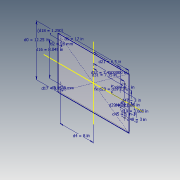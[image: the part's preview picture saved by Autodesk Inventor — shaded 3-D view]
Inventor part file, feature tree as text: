
AUTODESK INVENTOR PART (.ipt)
format: ipt  version: 2020.3 (Build 243373000, 373)  size: 146,944 bytes
history: native  units: in
note: dims shown in document units (in); Inventor stores cm internally (conversion verified against a paired STEP export)
features: hole x4, sketch x1, extrude x1, fillet x1
ambient origin geometry x8: Origin, YZ Plane, XZ Plane, XY Plane, X Axis, Y Axis, Z Axis, Center Point
bodies: Solid1 (feature_tree)
feature tree (7):
  sketch  "Sketch1"  dims[d0=12.25in d1=17.0in d2=1.1024in d3=1.1024in d4=8.0in d7=0.25in d8=0.0in d9=0.16in d10=0.75in d11=0.375in d12=0.25in d13=0.5635in d14=1.0in d15=0.8108in d16=8.045in d17=0.75in d18=1.2503in d19=3.688in d20=1.844in d21=6.5in d22=0.16in d23=0.75in d24=0.375in d25=0.25in d26=0.5635in d27=1.0in d28=0.8108in d29=0.8661in d31=7.35in d32=0.123in d33=0.75in d34=0.375in d35=0.25in d36=0.5635in d37=1.0in d38=0.8108in d40=0.375in d44=1.0in d45=1.0in d46=0.95in d47=3.0in d48=3.0in d49=0.177in d50=0.75in d51=0.37in d52=0.25in d53=90.0deg d54=1.0in d55=0.8108in d57=7.45in]
  extrude  "Extrusion1"  Depth=17.0in
  hole  "Hole1-Tap M5"  [1 undecoded]
  hole  "Hole2-Tap M5"  [1 undecoded]
  hole  "Hole3-Tap M4"  [1 undecoded]
  fillet  "Fillet1"  Radius=0.25in
  hole  "Hole4 CSINK M4"  [1 undecoded]
note: 4 required parameter values undecoded (feature->parameter linkage not recoverable at this tier; creation-order binding heuristic only, values carry confidence <= 0.55)
